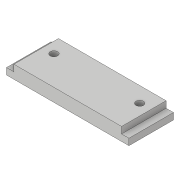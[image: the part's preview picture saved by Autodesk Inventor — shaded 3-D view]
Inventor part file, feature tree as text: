
AUTODESK INVENTOR PART (.ipt)
format: ipt  version: 2018.3 (Build 223284000, 284)  size: 104,960 bytes
history: native  units: in
note: dims shown in document units (in); Inventor stores cm internally (conversion verified against a paired STEP export)
features: extrude x3, sketch x3
ambient origin geometry x8: Origin, YZ Plane, XZ Plane, XY Plane, X Axis, Y Axis, Z Axis, Center Point
bodies: Solid1 (feature_tree)
feature tree (6):
  extrude  "Extrusion1"  Depth=0.756in
  extrude  "Extrusion6"  Depth=0.221in
  extrude  "Extrusion7"  Depth=0.1105in
  sketch  "Sketch1"  dims[d0=2.079in d1=0.756in]
  sketch  "Sketch7"  dims[d2=0.221in d3=0.0in d22=0.126in]
  sketch  "Sketch8"  dims[d23=0.126in d24=1.4567in d28=0.3112in d29=0.3112in d32=1.0in d33=0.0in d34=0.125in d35=0.125in d36=0.1105in d37=0.0in d38=0.4941in]
